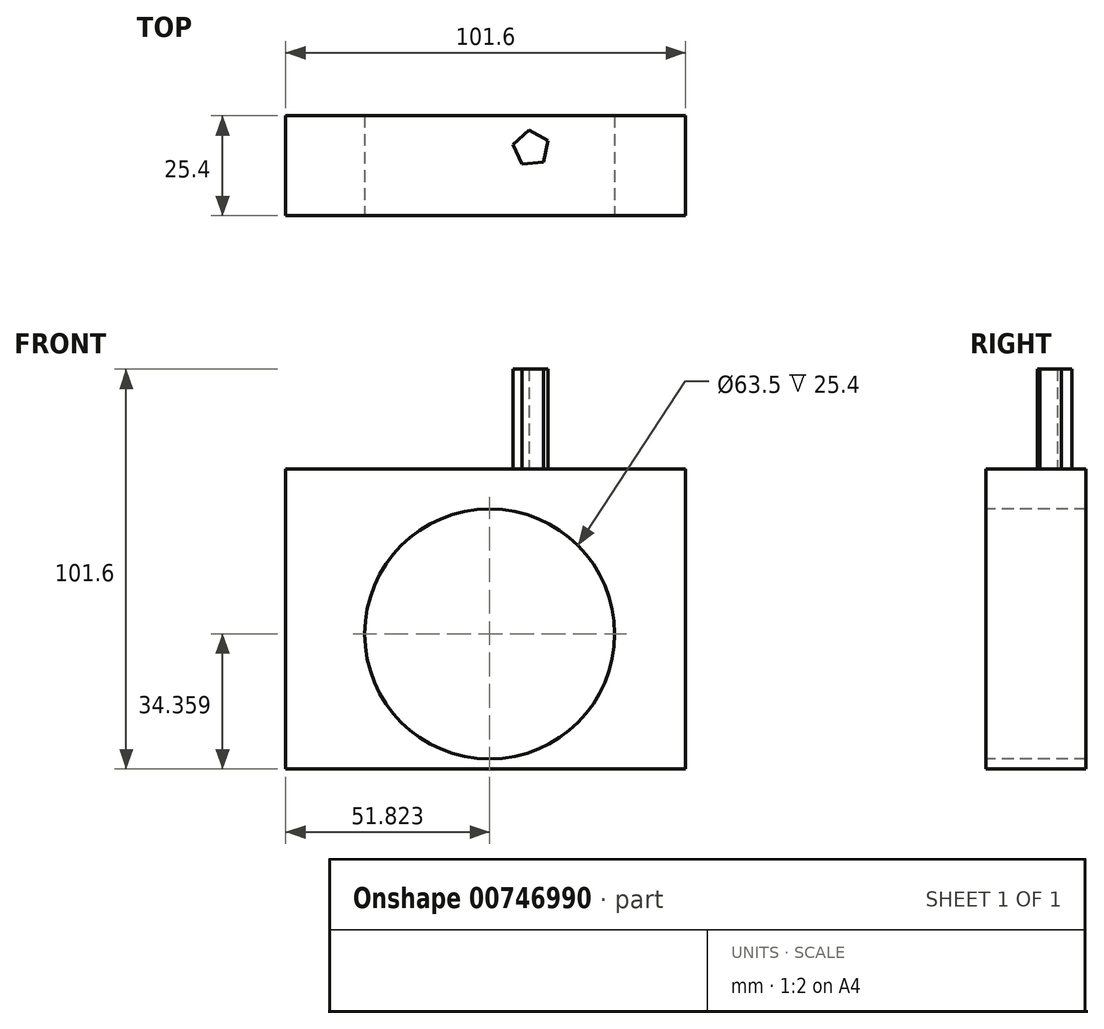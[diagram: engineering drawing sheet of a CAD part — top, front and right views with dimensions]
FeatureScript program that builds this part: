
annotation { "Feature Type Name" : "Feature", "Feature Type Description" : "" }
export const myFeature = defineFeature(function(context is Context, id is Id, definition is map)
    precondition{}
    {
        {
            var Q0;
            Q0=qCreatedBy(makeId("Front.planeOp"),FACE);
            var sketch = newSketch(context, id + "F0", { "sketchPlane" : qUnion([Q0])});
            skLineSegment(sketch, "E0.bottom", {"start": v(0, 0) * mm, "end": v(101.6, 0) * mm});
            skLineSegment(sketch, "E0.top", {"start": v(0, 76.2) * mm, "end": v(101.6, 76.2) * mm});
            skLineSegment(sketch, "E0.left", {"start": v(0, 0) * mm, "end": v(0, 76.2) * mm});
            skLineSegment(sketch, "E0.right", {"start": v(101.6, 0) * mm, "end": v(101.6, 76.2) * mm});
            skSolve(sketch);
        }
        {
            var Q0;
            Q0=makeQuery(id+"F0.imprint","IMPRINT",FACE,{"disambiguationData":[TD([[makeQuery(id+"F0.imprint","IMPRINT",EDGE,{"derivedFrom":sQuery(id+"F0.wireOp",EDGE,"E0.bottom")}),1.0]])]});
            extrude(context, id + "F1", {"entities" : qUnion([Q0]), "depth" : 25.4 * mm, "offsetDistance" : 25.4 * mm});
        }
        {
            var Q0;
            Q0=makeQuery(id+"F1.opExtrude","CAP_FACE",FACE,{"disambiguationData":[OSD([sQuery(id+"F0.wireOp",EDGE,"E0.bottom"),sQuery(id+"F0.wireOp",EDGE,"E0.top"),sQuery(id+"F0.wireOp",EDGE,"E0.left"),sQuery(id+"F0.wireOp",EDGE,"E0.right")])],"isStart":false});
            var sketch = newSketch(context, id + "F2", { "sketchPlane" : qUnion([Q0])});
            skCircle(sketch, "E1", {"center": v(51.82, 34.36) * mm, "radius": 16.92 * mm});
            skSolve(sketch);
        }
        {
            var Q0;
            Q0=sQuery(id+"F2.wireOp",VERTEX,"E1.center");
            var Q1;
            Q1=makeQuery(id+"F1.opExtrude","SWEPT_BODY",BODY,{"disambiguationData":[OSD([sQuery(id+"F0.wireOp",EDGE,"E0.bottom"),sQuery(id+"F0.wireOp",EDGE,"E0.top"),sQuery(id+"F0.wireOp",EDGE,"E0.left"),sQuery(id+"F0.wireOp",EDGE,"E0.right")])]});
            hole(context, id + "F3", {"style" : HoleStyle.SIMPLE, "endStyle" : HoleEndStyle.THROUGH, "holeDiameter" : 63.5 * mm, "majorDiameter" : 6.35 * mm, "isTappedThrough" : true, "tappedDepth" : 12.7 * mm, "tapClearance" : 3, "locations" : qUnion([Q0]), "scope" : qUnion([Q1])});
        }
        {
            var Q0;
            Q0=makeQuery(id+"F1.opExtrude","SWEPT_FACE",FACE,{"disambiguationData":[OSD([sQuery(id+"F0.wireOp",EDGE,"E0.top")])]});
            var sketch = newSketch(context, id + "F4", { "sketchPlane" : qUnion([Q0])});
            skCircle(sketch, "E2.cCircle", {"center": v(62.36, -8.26) * mm, "radius": 3.79 * mm, "construction": true});
            skLineSegment(sketch, "E2.0", {"start": v(57.77, -7.32) * mm, "end": v(61.83, -3.6) * mm});
            skLineSegment(sketch, "E2.1", {"start": v(61.83, -3.6) * mm, "end": v(66.62, -6.32) * mm});
            skLineSegment(sketch, "E2.2", {"start": v(66.62, -6.32) * mm, "end": v(65.52, -11.7) * mm});
            skLineSegment(sketch, "E2.3", {"start": v(65.52, -11.7) * mm, "end": v(60.05, -12.33) * mm});
            skLineSegment(sketch, "E2.4", {"start": v(60.05, -12.33) * mm, "end": v(57.77, -7.32) * mm});
            skPoint(sketch, "E2.0.midPoint", {"position": v(59.8, -5.47) * mm});
            skSolve(sketch);
        }
        {
            var Q0;
            Q0=makeQuery(id+"F4.imprint","IMPRINT",FACE,{"disambiguationData":[TD([[makeQuery(id+"F4.imprint","IMPRINT",EDGE,{"derivedFrom":sQuery(id+"F4.wireOp",EDGE,"E2.0")}),-1.0]])]});
            extrude(context, id + "F5", {"entities" : qUnion([Q0]), "operationType" : NewBodyOperationType.ADD, "depth" : 25.4 * mm, "offsetDistance" : 25.4 * mm});
        }
    });
